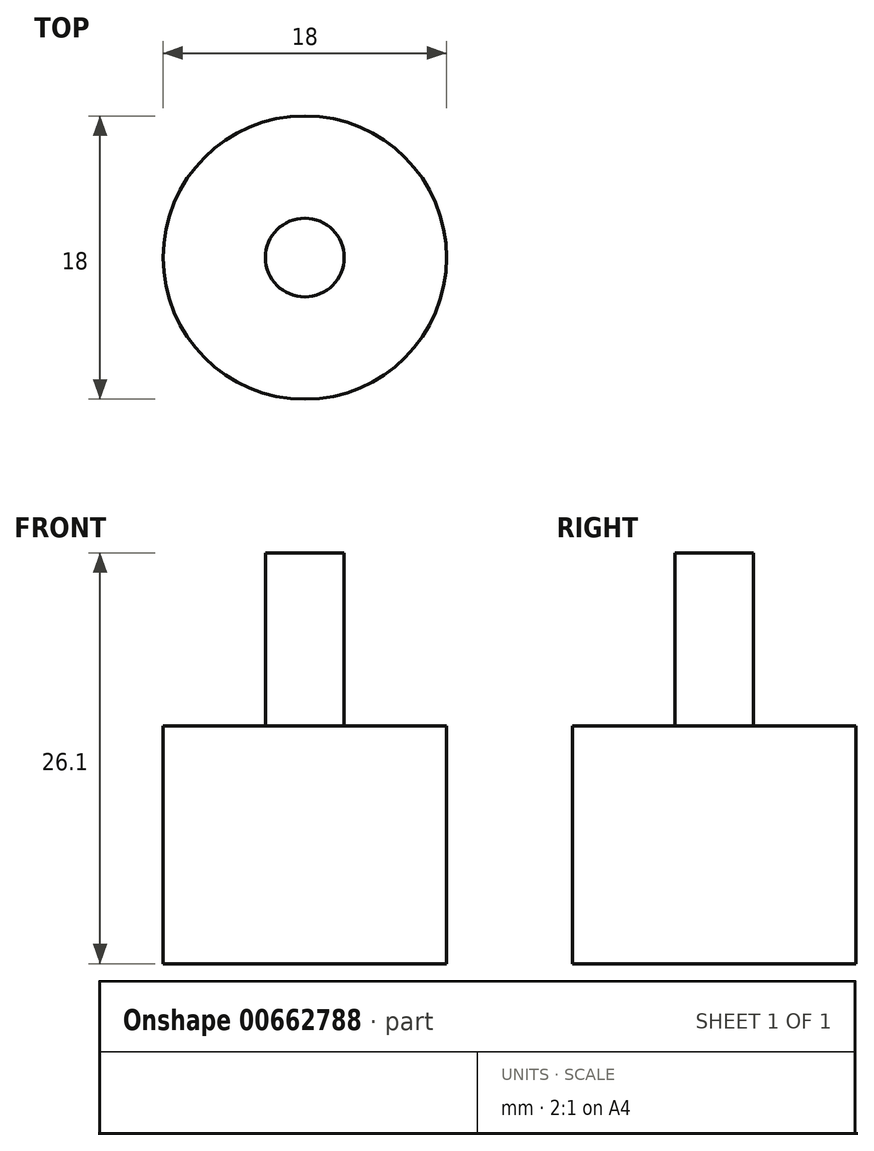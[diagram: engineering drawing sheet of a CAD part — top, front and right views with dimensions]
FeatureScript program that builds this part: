
annotation { "Feature Type Name" : "Feature", "Feature Type Description" : "" }
export const myFeature = defineFeature(function(context is Context, id is Id, definition is map)
    precondition{}
    {
        {
            var Q0;
            Q0=qCreatedBy(makeId("Front.planeOp"),FACE);
            var sketch = newSketch(context, id + "F0", { "sketchPlane" : qUnion([Q0])});
            skLineSegment(sketch, "E0", {"start": v(0, 0) * mm, "end": v(-9, 0) * mm});
            skLineSegment(sketch, "E1", {"start": v(-9, 0) * mm, "end": v(-9, 15.1) * mm});
            skLineSegment(sketch, "E2", {"start": v(0, 26.1) * mm, "end": v(0, 0) * mm});
            skLineSegment(sketch, "E3", {"start": v(-9, 15.1) * mm, "end": v(-2.5, 15.1) * mm});
            skLineSegment(sketch, "E4", {"start": v(-2.5, 15.1) * mm, "end": v(-2.5, 26.1) * mm});
            skLineSegment(sketch, "E5", {"start": v(-2.5, 26.1) * mm, "end": v(0, 26.1) * mm});
            skSolve(sketch);
        }
        {
            var Q0;
            Q0 = qSketchRegion(id + "F0", true);
            var Q1;
            Q1=sQuery(id+"F0.wireOp",EDGE,"E2");
            revolve(context, id + "F1", {"entities" : qUnion([Q0]), "axis" : qUnion([Q1]), "revolveType" : RevolveType.FULL});
        }
    });
